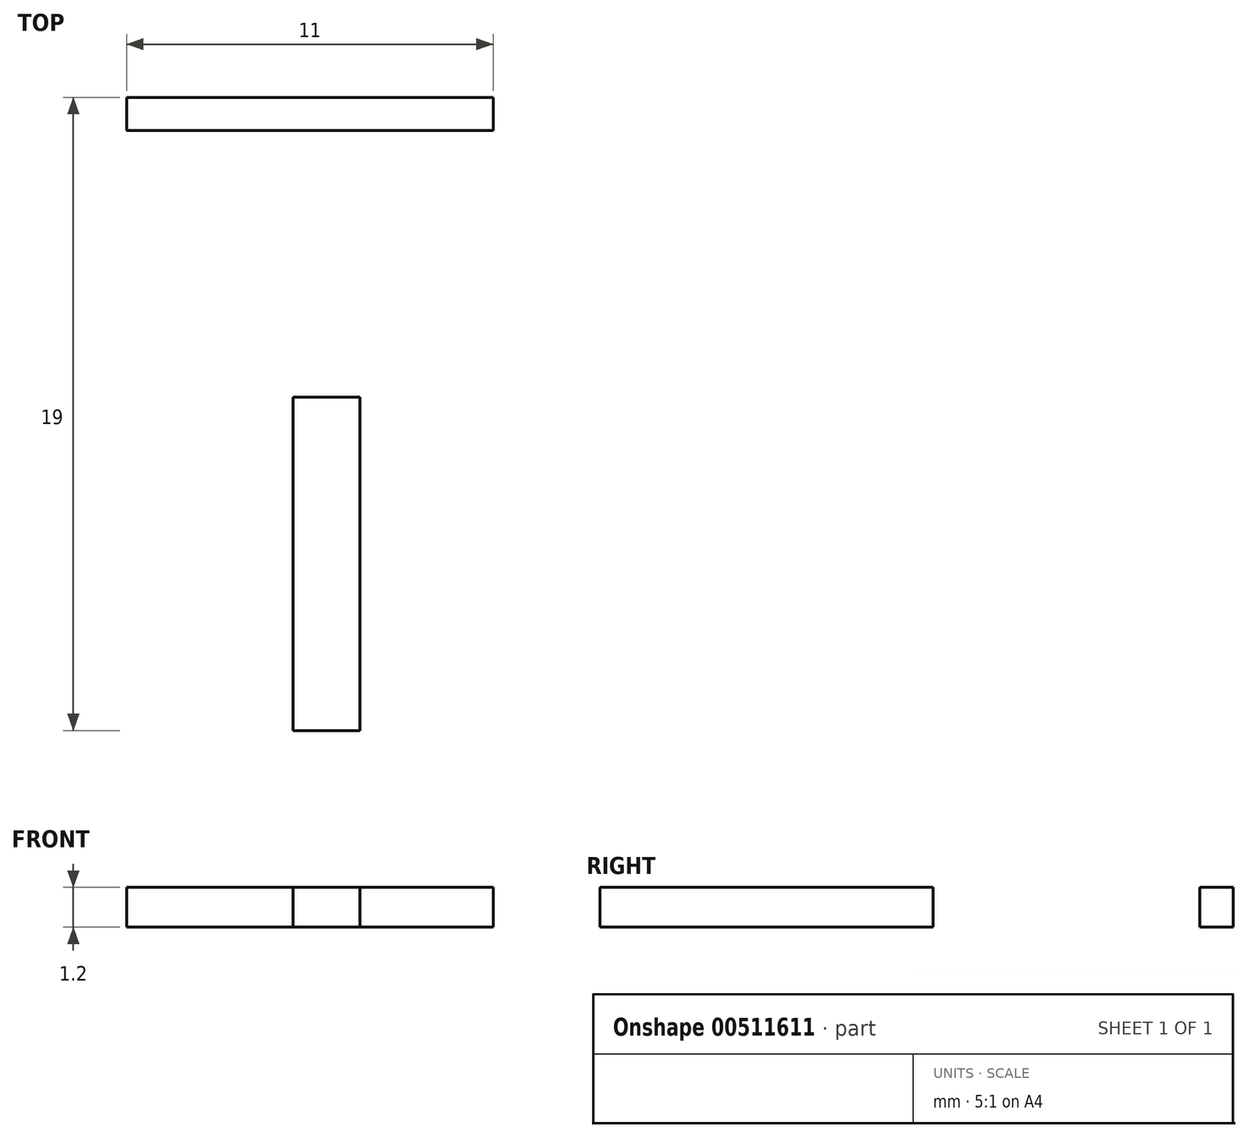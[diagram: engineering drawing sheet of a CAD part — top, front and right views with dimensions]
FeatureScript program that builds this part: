
annotation { "Feature Type Name" : "Feature", "Feature Type Description" : "" }
export const myFeature = defineFeature(function(context is Context, id is Id, definition is map)
    precondition{}
    {
        {
            var Q0;
            Q0=qCreatedBy(makeId("Top.planeOp"),FACE);
            var sketch = newSketch(context, id + "F0", { "sketchPlane" : qUnion([Q0])});
            skLineSegment(sketch, "E0.bottom", {"start": v(1, 2.5) * mm, "end": v(-1, 2.5) * mm});
            skLineSegment(sketch, "E0.top", {"start": v(1, -2.5) * mm, "end": v(-1, -2.5) * mm});
            skLineSegment(sketch, "E0.left", {"start": v(1, 2.5) * mm, "end": v(1, -2.5) * mm});
            skLineSegment(sketch, "E0.right", {"start": v(-1, 2.5) * mm, "end": v(-1, -2.5) * mm});
            skPoint(sketch, "E0.middle", {"position": v(0, 0) * mm});
            skLineSegment(sketch, "E1.top", {"start": v(1, 7.5) * mm, "end": v(-1, 7.5) * mm});
            skLineSegment(sketch, "E1.left", {"start": v(1, -2.5) * mm, "end": v(1, 7.5) * mm});
            skLineSegment(sketch, "E1.right", {"start": v(-1, -2.5) * mm, "end": v(-1, 7.5) * mm});
            skLineSegment(sketch, "E2", {"start": v(-1, 7.5) * mm, "end": v(-1, 15.5) * mm});
            skLineSegment(sketch, "E3", {"start": v(-1, 15.5) * mm, "end": v(5, 15.5) * mm});
            skLineSegment(sketch, "E4", {"start": v(5, 15.5) * mm, "end": v(5, 16.5) * mm});
            skLineSegment(sketch, "E5", {"start": v(5, 16.5) * mm, "end": v(-6, 16.5) * mm});
            skLineSegment(sketch, "E6", {"start": v(-6, 16.5) * mm, "end": v(-6, 15.5) * mm});
            skLineSegment(sketch, "E7", {"start": v(-6, 15.5) * mm, "end": v(-1, 15.5) * mm});
            skSolve(sketch);
        }
        {
            var Q0;
            Q0 = qSketchRegion(id + "F0", true);
            extrude(context, id + "F1", {"entities" : qUnion([Q0]), "depth" : 1.2 * mm, "offsetDistance" : 25 * mm});
        }
    });
